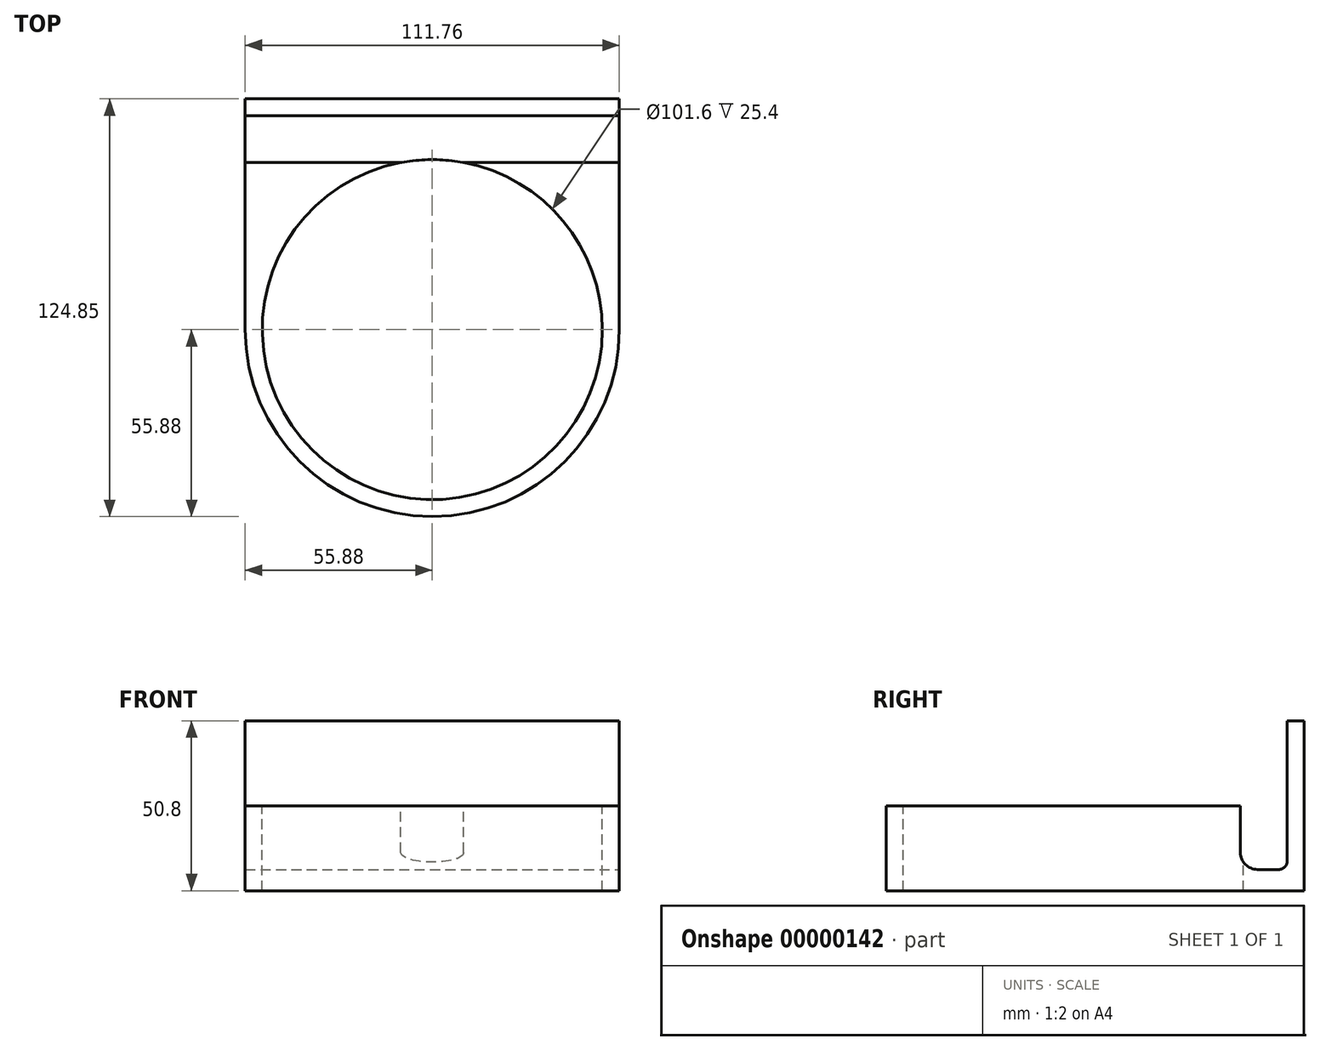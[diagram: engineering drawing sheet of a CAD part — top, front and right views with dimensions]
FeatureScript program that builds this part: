
annotation { "Feature Type Name" : "Feature", "Feature Type Description" : "" }
export const myFeature = defineFeature(function(context is Context, id is Id, definition is map)
    precondition{}
    {
        {
            var Q0;
            Q0=qCreatedBy(makeId("Top.planeOp"),FACE);
            var sketch = newSketch(context, id + "F0", { "sketchPlane" : qUnion([Q0])});
            skCircle(sketch, "E0", {"center": v(0, 0) * mm, "radius": 50.8 * mm});
            skCircle(sketch, "E1", {"center": v(0, 0) * mm, "radius": 55.88 * mm});
            skPoint(sketch, "E2.rect.middle", {"position": v(0, 59.45) * mm});
            skLineSegment(sketch, "E3.rect.bottom", {"start": v(-55.88, 68.97) * mm, "end": v(55.88, 68.97) * mm});
            skLineSegment(sketch, "E3.rect.top", {"start": v(-55.88, 49.92) * mm, "end": v(55.88, 49.92) * mm});
            skLineSegment(sketch, "E3.rect.left", {"start": v(-55.88, 68.97) * mm, "end": v(-55.88, 49.92) * mm});
            skLineSegment(sketch, "E3.rect.right", {"start": v(55.88, 68.97) * mm, "end": v(55.88, 49.92) * mm});
            skLineSegment(sketch, "E4", {"start": v(55.88, 49.92) * mm, "end": v(55.88, 0) * mm});
            skLineSegment(sketch, "E5", {"start": v(-55.88, 63.9) * mm, "end": v(55.88, 63.9) * mm});
            skLineSegment(sketch, "E6", {"start": v(-55.88, 55.88) * mm, "end": v(55.88, 55.88) * mm});
            skLineSegment(sketch, "E7", {"start": v(-55.88, 49.92) * mm, "end": v(-55.88, 0) * mm});
            skSolve(sketch);
        }
        {
            var Q0;
            {var subQ1=sQuery(id+"F0.wireOp",EDGE,"E5");var subQ3=sQuery(id+"F0.wireOp",EDGE,"E3.rect.bottom");var subQ4=makeQuery(id+"F0.imprint","IMPRINT",EDGE,{"derivedFrom":subQ1});var subQ7=sQuery(id+"F0.wireOp",EDGE,"E4");var subQ8=sQuery(id+"F0.wireOp",EDGE,"E3.rect.top");var subQ9=sQuery(id+"F0.wireOp",EDGE,"E1");var subQ10=makeQuery(id+"F0.imprint","INTERSECT",VERTEX,{"disambiguationData":[OD(0.0)],"derivedFrom":[subQ9,subQ8]});var subQ15=sQuery(id+"F0.wireOp",EDGE,"E7");var subQ21=sQuery(id+"F0.wireOp",EDGE,"E6");var subQ22=makeQuery(id+"F0.imprint","INTERSECT",VERTEX,{"derivedFrom":[subQ9,subQ21]});var subQ27=sQuery(id+"F0.wireOp",EDGE,"E0");var subQ29=makeQuery(id+"F0.imprint","INTERSECT",VERTEX,{"disambiguationData":[OD(0.0)],"derivedFrom":[subQ27,subQ8]});Q0=qUnion([makeQuery(id+"F0.imprint","IMPRINT",FACE,{"disambiguationData":[TD([[makeQuery(id+"F0.imprint","IMPRINT",EDGE,{"derivedFrom":subQ3}),-1.0]])]}),makeQuery(id+"F0.imprint","IMPRINT",FACE,{"disambiguationData":[TD([[makeQuery(id+"F0.imprint","IMPRINT",EDGE,{"derivedFrom":subQ7}),-1.0]])]}),makeQuery(id+"F0.imprint","IMPRINT",FACE,{"disambiguationData":[TD([[makeQuery(id+"F0.imprint","IMPRINT",EDGE,{"derivedFrom":subQ15}),1.0]])]}),makeQuery(id+"F0.imprint","IMPRINT",FACE,{"disambiguationData":[TD([[makeQuery(id+"F0.imprint","IMPRINT",EDGE,{"disambiguationData":[TD([[subQ10,-1.0]])],"derivedFrom":subQ9}),-1.0]])]}),makeQuery(id+"F0.imprint","IMPRINT",FACE,{"disambiguationData":[TD([[makeQuery(id+"F0.imprint","IMPRINT",EDGE,{"disambiguationData":[TD([[subQ22,-1.0]])],"derivedFrom":subQ9}),-1.0]])]}),makeQuery(id+"F0.imprint","IMPRINT",FACE,{"disambiguationData":[TD([[subQ4,-1.0]])]}),makeQuery(id+"F0.imprint","IMPRINT",FACE,{"disambiguationData":[TD([[makeQuery(id+"F0.imprint","IMPRINT",EDGE,{"disambiguationData":[TD([[subQ29,-1.0]])],"derivedFrom":subQ27}),-1.0]])]})]);}
            var Q1;
            {var subQ0=sQuery(id+"F0.wireOp",EDGE,"E3.rect.top");var subQ3=sQuery(id+"F0.wireOp",EDGE,"E0");var subQ6=makeQuery(id+"F0.imprint","INTERSECT",VERTEX,{"disambiguationData":[OD(0.0)],"derivedFrom":[subQ3,subQ0]});Q1=makeQuery(id+"F0.imprint","IMPRINT",FACE,{"disambiguationData":[TD([[makeQuery(id+"F0.imprint","IMPRINT",EDGE,{"disambiguationData":[TD([[subQ6,1.0]])],"derivedFrom":subQ3}),-1.0]])]});}
            extrude(context, id + "F1", {"entities" : qUnion([Q0, Q1]), "oppositeDirection" : true, "depth" : 25.4 * mm});
        }
        {
            var Q0;
            {var subQ0=sQuery(id+"F0.wireOp",EDGE,"E3.rect.top");var subQ3=sQuery(id+"F0.wireOp",EDGE,"E0");var subQ6=makeQuery(id+"F0.imprint","INTERSECT",VERTEX,{"disambiguationData":[OD(0.0)],"derivedFrom":[subQ3,subQ0]});Q0=makeQuery(id+"F0.imprint","IMPRINT",FACE,{"disambiguationData":[TD([[makeQuery(id+"F0.imprint","IMPRINT",EDGE,{"disambiguationData":[TD([[subQ6,1.0]])],"derivedFrom":subQ3}),-1.0]])]});}
            var Q1;
            {var subQ0=sQuery(id+"F0.wireOp",EDGE,"E6");var subQ1=sQuery(id+"F0.wireOp",EDGE,"E1");var subQ2=makeQuery(id+"F0.imprint","INTERSECT",VERTEX,{"derivedFrom":[subQ1,subQ0]});Q1=makeQuery(id+"F0.imprint","IMPRINT",FACE,{"disambiguationData":[TD([[makeQuery(id+"F0.imprint","IMPRINT",EDGE,{"disambiguationData":[TD([[subQ2,-1.0]])],"derivedFrom":subQ1}),-1.0]])]});}
            var Q2;
            {var subQ1=sQuery(id+"F0.wireOp",EDGE,"E1");var subQ5=sQuery(id+"F0.wireOp",EDGE,"E3.rect.top");var subQ7=makeQuery(id+"F0.imprint","INTERSECT",VERTEX,{"disambiguationData":[OD(0.0)],"derivedFrom":[subQ1,subQ5]});Q2=makeQuery(id+"F0.imprint","IMPRINT",FACE,{"disambiguationData":[TD([[makeQuery(id+"F0.imprint","IMPRINT",EDGE,{"disambiguationData":[TD([[subQ7,-1.0]])],"derivedFrom":subQ1}),-1.0]])]});}
            var Q3;
            {var subQ4=sQuery(id+"F0.wireOp",EDGE,"E5");Q3=makeQuery(id+"F0.imprint","IMPRINT",FACE,{"disambiguationData":[TD([[makeQuery(id+"F0.imprint","IMPRINT",EDGE,{"derivedFrom":subQ4}),-1.0]])]});}
            extrude(context, id + "F2", {"entities" : qUnion([Q0, Q1, Q2, Q3]), "operationType" : NewBodyOperationType.REMOVE, "oppositeDirection" : true, "depth" : 19.05 * mm});
        }
        {
            var Q0;
            {var subQ0=sQuery(id+"F0.wireOp",EDGE,"E0");var subQ1=sQuery(id+"F0.wireOp",EDGE,"E3.rect.top");Q0=makeQuery(id+"F2.boolean.opBoolean","COPY",EDGE,{"derivedFrom":makeQuery(id+"F2.opExtrude","SWEPT_EDGE",EDGE,{"disambiguationData":[OSD([subQ0,subQ1]),TDD([makeQuery(id+"F0.imprint","INTERSECT",VERTEX,{"disambiguationData":[OD(0.0)],"derivedFrom":[subQ0,subQ1]})])]})});}
            var Q1;
            {var subQ0=sQuery(id+"F0.wireOp",EDGE,"E0");var subQ1=sQuery(id+"F0.wireOp",EDGE,"E3.rect.top");Q1=makeQuery(id+"F2.boolean.opBoolean","COPY",EDGE,{"derivedFrom":makeQuery(id+"F2.opExtrude","SWEPT_EDGE",EDGE,{"disambiguationData":[OSD([subQ0,subQ1]),TDD([makeQuery(id+"F0.imprint","INTERSECT",VERTEX,{"disambiguationData":[OD(1.0)],"derivedFrom":[subQ0,subQ1]})])]})});}
            var Q2;
            Q2=makeQuery(id+"F2.boolean.opBoolean","COPY",EDGE,{"derivedFrom":makeQuery(id+"F2.opExtrude","CAP_EDGE",EDGE,{"disambiguationData":[OSD([sQuery(id+"F0.wireOp",EDGE,"E5")])],"isStart":false})});
            fillet(context, id + "F3", {"entities" : qUnion([Q0, Q1, Q2]), "radius" : 2.54 * mm, "tangentPropagation" : true, "allowEdgeOverflow" : false});
        }
        {
            var Q0;
            {var subQ0=sQuery(id+"F0.wireOp",EDGE,"E3.rect.top");var subQ1=makeQuery(id+"F0.imprint","INTERSECT",VERTEX,{"disambiguationData":[OD(1.0)],"derivedFrom":[sQuery(id+"F0.wireOp",EDGE,"E1"),subQ0]});Q0=makeQuery(id+"F2.boolean.opBoolean","COPY",EDGE,{"derivedFrom":makeQuery(id+"F2.opExtrude","CAP_EDGE",EDGE,{"disambiguationData":[OSD([subQ0]),TDD([makeQuery(id+"F0.imprint","IMPRINT",EDGE,{"disambiguationData":[TD([[subQ1,1.0]])],"derivedFrom":subQ0}),makeQuery(id+"F0.imprint","IMPRINT",EDGE,{"disambiguationData":[TD([[makeQuery(id+"F0.imprint","INTERSECT",VERTEX,{"disambiguationData":[OD(0.0)],"derivedFrom":[sQuery(id+"F0.wireOp",EDGE,"E0"),subQ0]}),1.0]])],"derivedFrom":subQ0})])],"isStart":false})});}
            var Q1;
            {var subQ0=sQuery(id+"F0.wireOp",EDGE,"E3.rect.top");var subQ1=makeQuery(id+"F0.imprint","INTERSECT",VERTEX,{"disambiguationData":[OD(0.0)],"derivedFrom":[sQuery(id+"F0.wireOp",EDGE,"E1"),subQ0]});Q1=makeQuery(id+"F2.boolean.opBoolean","COPY",EDGE,{"derivedFrom":makeQuery(id+"F2.opExtrude","CAP_EDGE",EDGE,{"disambiguationData":[OSD([subQ0]),TDD([makeQuery(id+"F0.imprint","IMPRINT",EDGE,{"disambiguationData":[TD([[makeQuery(id+"F0.imprint","INTERSECT",VERTEX,{"disambiguationData":[OD(1.0)],"derivedFrom":[sQuery(id+"F0.wireOp",EDGE,"E0"),subQ0]}),-1.0]])],"derivedFrom":subQ0}),makeQuery(id+"F0.imprint","IMPRINT",EDGE,{"disambiguationData":[TD([[subQ1,-1.0]])],"derivedFrom":subQ0})])],"isStart":false})});}
            fillet(context, id + "F4", {"entities" : qUnion([Q0, Q1]), "radius" : 5.08 * mm, "tangentPropagation" : true, "allowEdgeOverflow" : false});
        }
        {
            var Q0;
            {var subQ2=sQuery(id+"F0.wireOp",EDGE,"E3.rect.bottom");Q0=makeQuery(id+"F0.imprint","IMPRINT",FACE,{"disambiguationData":[TD([[makeQuery(id+"F0.imprint","IMPRINT",EDGE,{"derivedFrom":subQ2}),-1.0]])]});}
            extrude(context, id + "F5", {"entities" : qUnion([Q0]), "operationType" : NewBodyOperationType.ADD, "depth" : 25.4 * mm});
        }
    });
